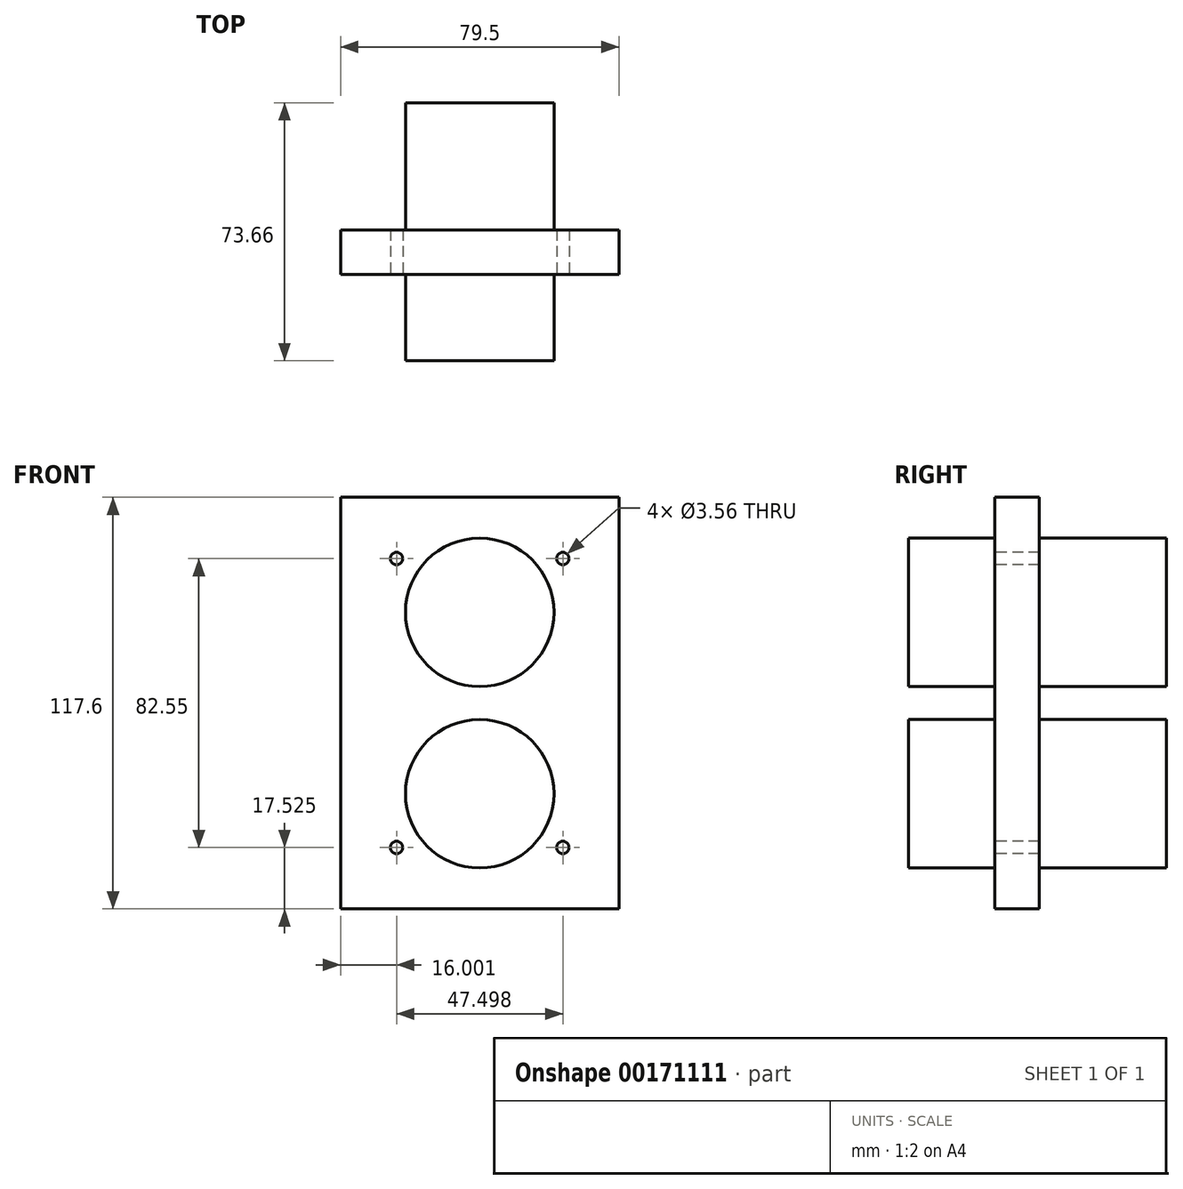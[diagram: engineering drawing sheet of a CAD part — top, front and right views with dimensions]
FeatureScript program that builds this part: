
annotation { "Feature Type Name" : "Feature", "Feature Type Description" : "" }
export const myFeature = defineFeature(function(context is Context, id is Id, definition is map)
    precondition{}
    {
        {
            var Q0;
            Q0=qCreatedBy(makeId("Front.planeOp"),FACE);
            var sketch = newSketch(context, id + "F0", { "sketchPlane" : qUnion([Q0])});
            skLineSegment(sketch, "E0.bottom", {"start": v(-39.75, 58.8) * mm, "end": v(39.75, 58.8) * mm});
            skLineSegment(sketch, "E0.top", {"start": v(-39.75, -58.8) * mm, "end": v(39.75, -58.8) * mm});
            skLineSegment(sketch, "E0.left", {"start": v(-39.75, 58.8) * mm, "end": v(-39.75, -58.8) * mm});
            skLineSegment(sketch, "E0.right", {"start": v(39.75, 58.8) * mm, "end": v(39.75, -58.8) * mm});
            skPoint(sketch, "E0.middle", {"position": v(0, 0) * mm});
            skSolve(sketch);
        }
        {
            var Q0;
            Q0 = qSketchRegion(id + "F0", true);
            extrude(context, id + "F1", {"entities" : qUnion([Q0]), "depth" : 12.7 * mm});
        }
        {
            var Q0;
            Q0=makeQuery(id+"F1.opExtrude","CAP_FACE",FACE,{"disambiguationData":[OSD([sQuery(id+"F0.wireOp",EDGE,"E0.bottom"),sQuery(id+"F0.wireOp",EDGE,"E0.top"),sQuery(id+"F0.wireOp",EDGE,"E0.left"),sQuery(id+"F0.wireOp",EDGE,"E0.right")])],"isStart":false});
            var sketch = newSketch(context, id + "F2", { "sketchPlane" : qUnion([Q0])});
            skCircle(sketch, "E1", {"center": v(-23.75, 41.28) * mm, "radius": 1.78 * mm});
            skCircle(sketch, "E2", {"center": v(23.75, 41.28) * mm, "radius": 1.78 * mm});
            skCircle(sketch, "E3", {"center": v(-23.75, -41.28) * mm, "radius": 1.78 * mm});
            skCircle(sketch, "E4", {"center": v(23.75, -41.28) * mm, "radius": 1.78 * mm});
            skSolve(sketch);
        }
        {
            var Q0;
            Q0 = qSketchRegion(id + "F2", true);
            extrude(context, id + "F3", {"entities" : qUnion([Q0]), "operationType" : NewBodyOperationType.REMOVE, "endBound" : BoundingType.THROUGH_ALL, "oppositeDirection" : true, "depth" : 25.4 * mm});
        }
        {
            var Q0;
            Q0=makeQuery(id+"F1.opExtrude","CAP_FACE",FACE,{"disambiguationData":[OSD([sQuery(id+"F0.wireOp",EDGE,"E0.bottom"),sQuery(id+"F0.wireOp",EDGE,"E0.top"),sQuery(id+"F0.wireOp",EDGE,"E0.left"),sQuery(id+"F0.wireOp",EDGE,"E0.right")])],"isStart":true});
            var sketch = newSketch(context, id + "F4", { "sketchPlane" : qUnion([Q0])});
            skCircle(sketch, "E5", {"center": v(0, 25.9) * mm, "radius": 21.2 * mm});
            skCircle(sketch, "E6", {"center": v(0, -25.9) * mm, "radius": 21.2 * mm});
            skSolve(sketch);
        }
        {
            var Q0;
            Q0 = qSketchRegion(id + "F4", true);
            extrude(context, id + "F5", {"entities" : qUnion([Q0]), "operationType" : NewBodyOperationType.ADD, "depth" : 36.32 * mm});
        }
        {
            var Q0;
            Q0=makeQuery(id+"F1.opExtrude","CAP_FACE",FACE,{"disambiguationData":[OSD([sQuery(id+"F0.wireOp",EDGE,"E0.bottom"),sQuery(id+"F0.wireOp",EDGE,"E0.top"),sQuery(id+"F0.wireOp",EDGE,"E0.left"),sQuery(id+"F0.wireOp",EDGE,"E0.right")])],"isStart":false});
            var sketch = newSketch(context, id + "F6", { "sketchPlane" : qUnion([Q0])});
            skCircle(sketch, "E7", {"center": v(0, 25.9) * mm, "radius": 21.2 * mm});
            skCircle(sketch, "E8", {"center": v(0, -25.9) * mm, "radius": 21.2 * mm});
            skSolve(sketch);
        }
        {
            var Q0;
            Q0 = qSketchRegion(id + "F6", true);
            extrude(context, id + "F7", {"entities" : qUnion([Q0]), "operationType" : NewBodyOperationType.ADD, "depth" : 24.64 * mm});
        }
    });
